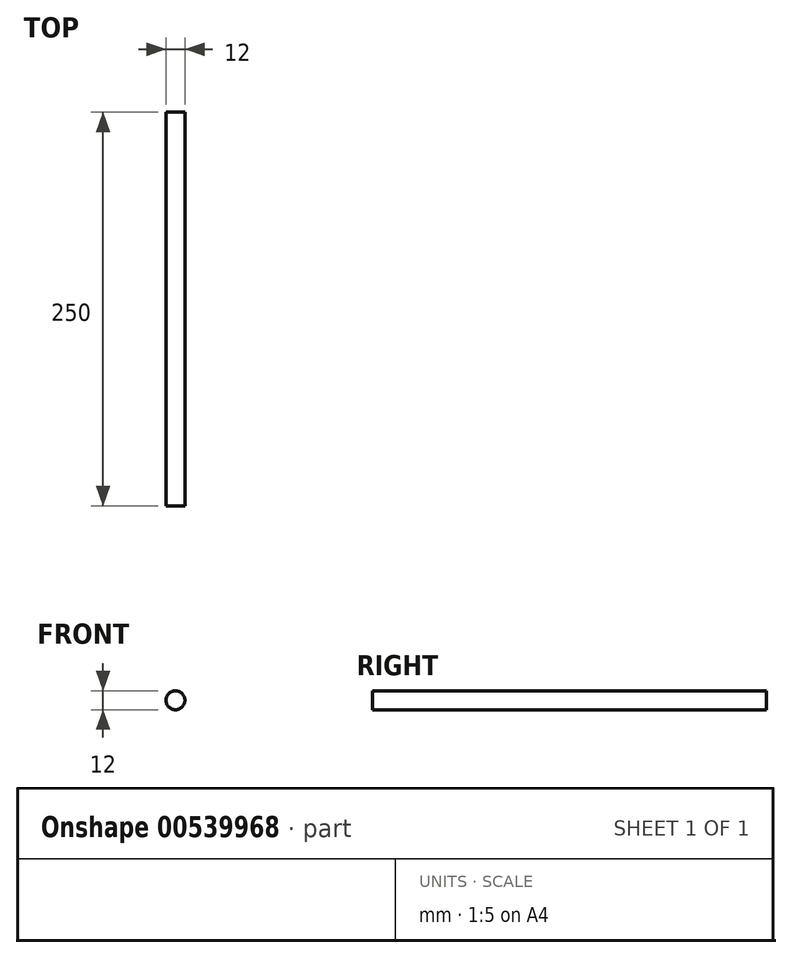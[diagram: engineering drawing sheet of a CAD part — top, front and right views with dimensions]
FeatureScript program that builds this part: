
annotation { "Feature Type Name" : "Feature", "Feature Type Description" : "" }
export const myFeature = defineFeature(function(context is Context, id is Id, definition is map)
    precondition{}
    {
        {
            var Q0;
            Q0=qCreatedBy(makeId("Front.planeOp"),FACE);
            var sketch = newSketch(context, id + "F0", { "sketchPlane" : qUnion([Q0])});
            skCircle(sketch, "E0", {"center": v(0, 0) * mm, "radius": 6 * mm});
            skSolve(sketch);
        }
        {
            var Q0;
            Q0=makeQuery(id+"F0.imprint","IMPRINT",FACE,{"disambiguationData":[TD([[makeQuery(id+"F0.imprint","IMPRINT",EDGE,{"derivedFrom":sQuery(id+"F0.wireOp",EDGE,"E0")}),1.0]])]});
            extrude(context, id + "F1", {"entities" : qUnion([Q0]), "depth" : 250 * mm, "offsetDistance" : 25 * mm});
        }
    });
